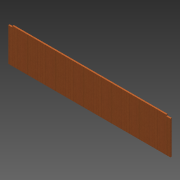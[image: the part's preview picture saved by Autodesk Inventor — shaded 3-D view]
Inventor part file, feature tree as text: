
AUTODESK INVENTOR PART (.ipt)
format: ipt  version: 2013 (Build 170138000, 138)  size: 83,456 bytes
history: native  units: in
note: dims shown in document units (in); Inventor stores cm internally (conversion verified against a paired STEP export)
features: extrude x1, sketch x1
ambient origin geometry x8: Origin, YZ Plane, XZ Plane, XY Plane, X Axis, Y Axis, Z Axis, Center Point
bodies: Solid1 (feature_tree)
feature tree (2):
  extrude  "Extrusion1"  Depth=12.0in
  sketch  "Sketch1"  dims[d0=58.0in d1=12.0in d2=0.5in d3=0.0in d4=0.5in d5=1.5in d6=1.5in]
